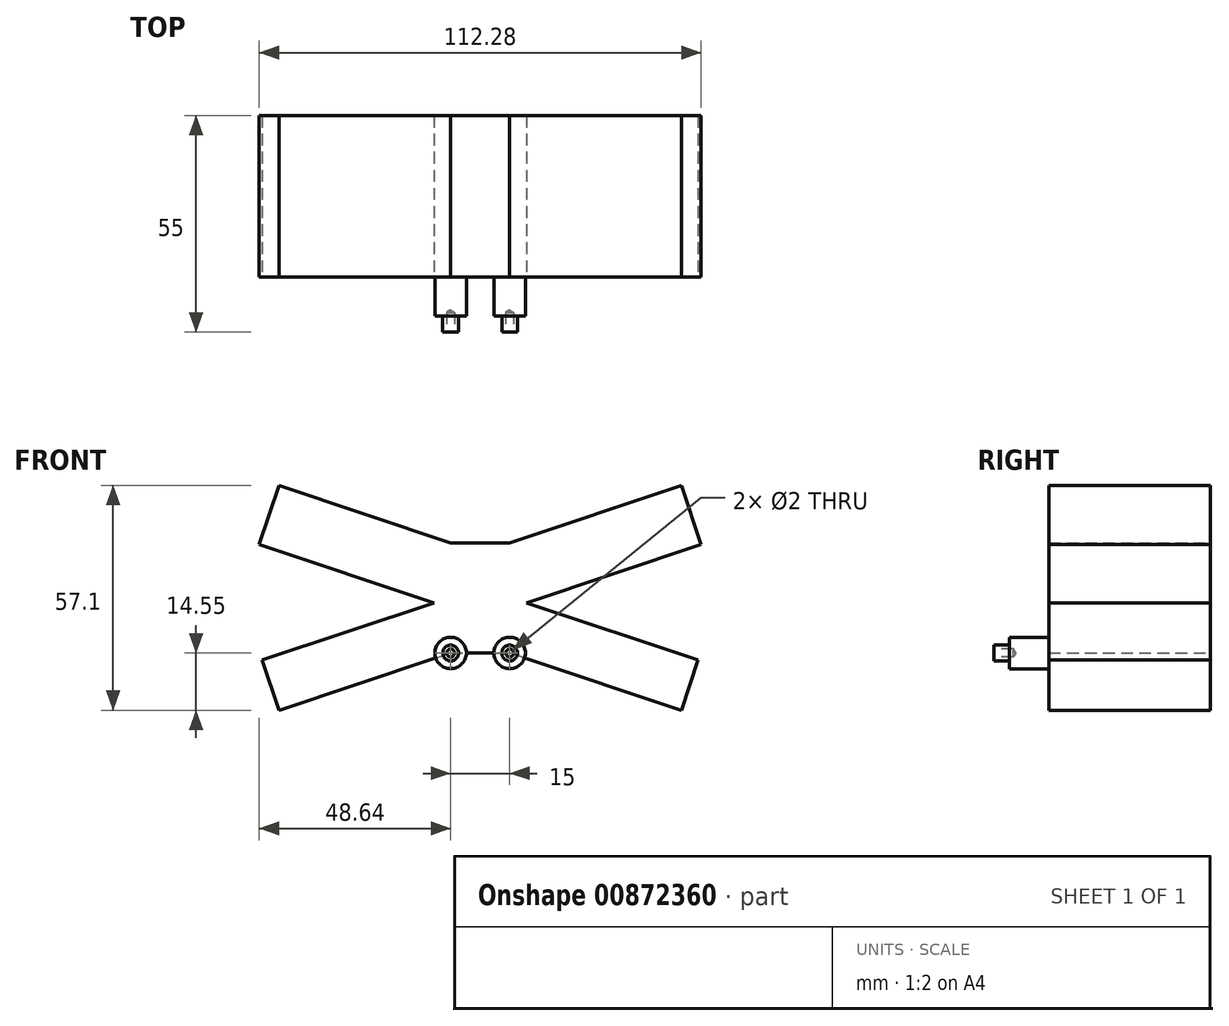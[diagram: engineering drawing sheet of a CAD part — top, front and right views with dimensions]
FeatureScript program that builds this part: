
annotation { "Feature Type Name" : "Feature", "Feature Type Description" : "" }
export const myFeature = defineFeature(function(context is Context, id is Id, definition is map)
    precondition{}
    {
        {
            var Q0;
            Q0=qCreatedBy(makeId("Front.planeOp"),FACE);
            var sketch = newSketch(context, id + "F0", { "sketchPlane" : qUnion([Q0])});
            skLineSegment(sketch, "E0.bottom", {"start": v(0, 0) * mm, "end": v(25, 0) * mm});
            skLineSegment(sketch, "E0.top", {"start": v(0, 28) * mm, "end": v(25, 28) * mm});
            skLineSegment(sketch, "E0.left", {"start": v(0, 0) * mm, "end": v(0, 28) * mm});
            skLineSegment(sketch, "E0.right", {"start": v(25, 0) * mm, "end": v(25, 28) * mm});
            skSolve(sketch);
        }
        {
            var Q0;
            Q0 = qSketchRegion(id + "F0", true);
            var Q1;
            Q1=makeQuery(id+"F0.imprint","IMPRINT",FACE,{"disambiguationData":[TD([[makeQuery(id+"F0.imprint","IMPRINT",EDGE,{"derivedFrom":sQuery(id+"F0.wireOp",EDGE,"E0.bottom")}),1.0]])]});
            extrude(context, id + "F1", {"entities" : qUnion([Q0, Q1]), "depth" : 41 * mm, "offsetDistance" : 25 * mm});
        }
        {
            var Q0;
            Q0=makeQuery(id+"F1.opExtrude","CAP_FACE",FACE,{"disambiguationData":[OSD([sQuery(id+"F0.wireOp",EDGE,"E0.bottom"),sQuery(id+"F0.wireOp",EDGE,"E0.top"),sQuery(id+"F0.wireOp",EDGE,"E0.left"),sQuery(id+"F0.wireOp",EDGE,"E0.right")])],"isStart":false});
            var sketch = newSketch(context, id + "F2", { "sketchPlane" : qUnion([Q0])});
            skCircle(sketch, "E1", {"center": v(25, 0) * mm, "radius": 3.5 * mm});
            skCircle(sketch, "E2", {"center": v(0, 0) * mm, "radius": 3.5 * mm});
            skSolve(sketch);
        }
        {
            var Q0;
            {var subQ0=sQuery(id+"F2.wireOp",EDGE,"E2");var subQ1=makeQuery(id+"F1.opExtrude","CAP_EDGE",EDGE,{"disambiguationData":[OSD([sQuery(id+"F0.wireOp",EDGE,"E0.bottom")])],"isStart":false});var subQ2=makeQuery(id+"F2.imprint","INTERSECT",VERTEX,{"derivedFrom":[subQ1,subQ0]});Q0=makeQuery(id+"F2.imprint","IMPRINT",FACE,{"disambiguationData":[TD([[makeQuery(id+"F2.imprint","IMPRINT",EDGE,{"disambiguationData":[TD([[subQ2,1.0]])],"derivedFrom":subQ0}),1.0]])]});}
            var Q1;
            {var subQ0=sQuery(id+"F2.wireOp",EDGE,"E2");var subQ1=makeQuery(id+"F1.opExtrude","CAP_EDGE",EDGE,{"disambiguationData":[OSD([sQuery(id+"F0.wireOp",EDGE,"E0.bottom")])],"isStart":false});var subQ2=makeQuery(id+"F2.imprint","INTERSECT",VERTEX,{"derivedFrom":[subQ1,subQ0]});Q1=makeQuery(id+"F2.imprint","IMPRINT",FACE,{"disambiguationData":[TD([[makeQuery(id+"F2.imprint","IMPRINT",EDGE,{"disambiguationData":[TD([[subQ2,-1.0]])],"derivedFrom":subQ0}),1.0]])]});}
            var Q2;
            {var subQ0=sQuery(id+"F2.wireOp",EDGE,"E1");var subQ1=makeQuery(id+"F1.opExtrude","CAP_EDGE",EDGE,{"disambiguationData":[OSD([sQuery(id+"F0.wireOp",EDGE,"E0.bottom")])],"isStart":false});var subQ2=makeQuery(id+"F2.imprint","INTERSECT",VERTEX,{"derivedFrom":[subQ1,subQ0]});Q2=makeQuery(id+"F2.imprint","IMPRINT",FACE,{"disambiguationData":[TD([[makeQuery(id+"F2.imprint","IMPRINT",EDGE,{"disambiguationData":[TD([[subQ2,-1.0]])],"derivedFrom":subQ0}),1.0]])]});}
            var Q3;
            {var subQ0=sQuery(id+"F2.wireOp",EDGE,"E1");var subQ1=makeQuery(id+"F1.opExtrude","CAP_EDGE",EDGE,{"disambiguationData":[OSD([sQuery(id+"F0.wireOp",EDGE,"E0.bottom")])],"isStart":false});var subQ2=makeQuery(id+"F2.imprint","INTERSECT",VERTEX,{"derivedFrom":[subQ1,subQ0]});Q3=makeQuery(id+"F2.imprint","IMPRINT",FACE,{"disambiguationData":[TD([[makeQuery(id+"F2.imprint","IMPRINT",EDGE,{"disambiguationData":[TD([[subQ2,1.0]])],"derivedFrom":subQ0}),1.0]])]});}
            extrude(context, id + "F3", {"entities" : qUnion([Q0, Q1, Q2, Q3]), "operationType" : NewBodyOperationType.ADD, "depth" : 8 * mm, "offsetDistance" : 25 * mm});
        }
        {
            var Q0;
            Q0=makeQuery(id+"F3.opExtrude","CAP_FACE",FACE,{"disambiguationData":[OSD([sQuery(id+"F2.wireOp",EDGE,"E2")])],"isStart":false});
            var sketch = newSketch(context, id + "F4", { "sketchPlane" : qUnion([Q0])});
            skCircle(sketch, "E3", {"center": v(0, 0) * mm, "radius": 2 * mm});
            skSolve(sketch);
        }
        {
            var Q0;
            Q0=makeQuery(id+"F4.imprint","IMPRINT",FACE,{"disambiguationData":[TD([[makeQuery(id+"F4.imprint","IMPRINT",EDGE,{"derivedFrom":sQuery(id+"F4.wireOp",EDGE,"E3")}),1.0]])]});
            extrude(context, id + "F5", {"entities" : qUnion([Q0]), "operationType" : NewBodyOperationType.ADD, "depth" : 5 * mm, "offsetDistance" : 25 * mm});
        }
        {
            var Q0;
            Q0=makeQuery(id+"F3.opExtrude","CAP_FACE",FACE,{"disambiguationData":[OSD([sQuery(id+"F2.wireOp",EDGE,"E1")])],"isStart":false});
            var sketch = newSketch(context, id + "F6", { "sketchPlane" : qUnion([Q0])});
            skCircle(sketch, "E4", {"center": v(25, 0) * mm, "radius": 2 * mm});
            skSolve(sketch);
        }
        {
            var Q0;
            Q0=makeQuery(id+"F6.imprint","IMPRINT",FACE,{"disambiguationData":[TD([[makeQuery(id+"F6.imprint","IMPRINT",EDGE,{"derivedFrom":sQuery(id+"F6.wireOp",EDGE,"E4")}),1.0]])]});
            extrude(context, id + "F7", {"entities" : qUnion([Q0]), "operationType" : NewBodyOperationType.ADD, "depth" : 5 * mm, "offsetDistance" : 25 * mm});
        }
        {
            var Q0;
            Q0=makeQuery(id+"F5.opExtrude","CAP_FACE",FACE,{"disambiguationData":[OSD([sQuery(id+"F4.wireOp",EDGE,"E3")])],"isStart":false});
            var sketch = newSketch(context, id + "F8", { "sketchPlane" : qUnion([Q0])});
            skCircle(sketch, "E5", {"center": v(0, 0) * mm, "radius": 1 * mm});
            skSolve(sketch);
        }
        {
            var Q0;
            Q0=sQuery(id+"F8.wireOp",VERTEX,"E5.center");
            var Q1;
            Q1=makeQuery(id+"F1.opExtrude","SWEPT_BODY",BODY,{"disambiguationData":[OSD([sQuery(id+"F0.wireOp",EDGE,"E0.bottom"),sQuery(id+"F0.wireOp",EDGE,"E0.top"),sQuery(id+"F0.wireOp",EDGE,"E0.left"),sQuery(id+"F0.wireOp",EDGE,"E0.right")])]});
            hole(context, id + "F9", {"style" : HoleStyle.SIMPLE, "endStyle" : HoleEndStyle.BLIND, "holeDiameter" : 2 * mm, "majorDiameter" : 5 * mm, "holeDepth" : 5 * mm, "isTappedThrough" : true, "tappedDepth" : 12 * mm, "tapClearance" : 3, "locations" : qUnion([Q0]), "scope" : qUnion([Q1])});
        }
        {
            var Q0;
            Q0=makeQuery(id+"F7.opExtrude","CAP_FACE",FACE,{"disambiguationData":[OSD([sQuery(id+"F6.wireOp",EDGE,"E4")])],"isStart":false});
            var sketch = newSketch(context, id + "F10", { "sketchPlane" : qUnion([Q0])});
            skCircle(sketch, "E6", {"center": v(25, 0) * mm, "radius": 1 * mm});
            skSolve(sketch);
        }
        {
            var Q0;
            Q0=sQuery(id+"F10.wireOp",VERTEX,"E6.center");
            var Q1;
            Q1=makeQuery(id+"F1.opExtrude","SWEPT_BODY",BODY,{"disambiguationData":[OSD([sQuery(id+"F0.wireOp",EDGE,"E0.bottom"),sQuery(id+"F0.wireOp",EDGE,"E0.top"),sQuery(id+"F0.wireOp",EDGE,"E0.left"),sQuery(id+"F0.wireOp",EDGE,"E0.right")])]});
            hole(context, id + "F11", {"style" : HoleStyle.SIMPLE, "endStyle" : HoleEndStyle.BLIND, "holeDiameter" : 2 * mm, "majorDiameter" : 5 * mm, "holeDepth" : 5 * mm, "isTappedThrough" : true, "tappedDepth" : 12 * mm, "tapClearance" : 3, "locations" : qUnion([Q0]), "scope" : qUnion([Q1])});
        }
        {
            var Q0;
            Q0=makeQuery(id+"F1.opExtrude","SWEPT_EDGE",EDGE,{"disambiguationData":[OSD([sQuery(id+"F0.wireOp",EDGE,"E0.top"),sQuery(id+"F0.wireOp",EDGE,"E0.left")])]});
            chamfer(context, id + "F12", {"entities" : qUnion([Q0]), "chamferType" : ChamferType.TWO_OFFSETS, "width1" : 15 * mm, "oppositeDirection" : false, "width2" : 5 * mm, "tangentPropagation" : true});
        }
        {
            var Q0;
            Q0=makeQuery(id+"F1.opExtrude","SWEPT_EDGE",EDGE,{"disambiguationData":[OSD([sQuery(id+"F0.wireOp",EDGE,"E0.top"),sQuery(id+"F0.wireOp",EDGE,"E0.right")])]});
            chamfer(context, id + "F13", {"entities" : qUnion([Q0]), "chamferType" : ChamferType.TWO_OFFSETS, "width1" : 5 * mm, "oppositeDirection" : false, "width2" : 15 * mm, "tangentPropagation" : true});
        }
        {
            var Q0;
            Q0=makeQuery(id+"F13.opChamfer","BLEND_FACE",FACE,{"disambiguationData":[OSD([sQuery(id+"F0.wireOp",EDGE,"E0.top"),sQuery(id+"F0.wireOp",EDGE,"E0.right")])]});
            var sketch = newSketch(context, id + "F14", { "sketchPlane" : qUnion([Q0])});
            skLineSegment(sketch, "E7.bottom", {"start": v(-41, 4.43) * mm, "end": v(0, 4.43) * mm});
            skLineSegment(sketch, "E7.top", {"start": v(-41, 20.24) * mm, "end": v(0, 20.24) * mm});
            skLineSegment(sketch, "E7.left", {"start": v(-41, 4.43) * mm, "end": v(-41, 20.24) * mm});
            skLineSegment(sketch, "E7.right", {"start": v(0, 4.43) * mm, "end": v(0, 20.24) * mm});
            skSolve(sketch);
        }
        {
            var Q0;
            Q0 = qSketchRegion(id + "F14", true);
            extrude(context, id + "F15", {"entities" : qUnion([Q0]), "operationType" : NewBodyOperationType.ADD, "depth" : 46 * mm, "offsetDistance" : 25 * mm});
        }
        {
            var Q0;
            Q0=makeQuery(id+"F12.opChamfer","BLEND_FACE",FACE,{"disambiguationData":[OSD([sQuery(id+"F0.wireOp",EDGE,"E0.top"),sQuery(id+"F0.wireOp",EDGE,"E0.left")])]});
            var sketch = newSketch(context, id + "F16", { "sketchPlane" : qUnion([Q0])});
            skLineSegment(sketch, "E8.bottom", {"start": v(0, 12.33) * mm, "end": v(41, 12.33) * mm});
            skLineSegment(sketch, "E8.top", {"start": v(0, 28.14) * mm, "end": v(41, 28.14) * mm});
            skLineSegment(sketch, "E8.left", {"start": v(0, 12.33) * mm, "end": v(0, 28.14) * mm});
            skLineSegment(sketch, "E8.right", {"start": v(41, 12.33) * mm, "end": v(41, 28.14) * mm});
            skSolve(sketch);
        }
        {
            var Q0;
            Q0 = qSketchRegion(id + "F16", true);
            extrude(context, id + "F17", {"entities" : qUnion([Q0]), "operationType" : NewBodyOperationType.ADD, "depth" : 46 * mm, "offsetDistance" : 25 * mm});
        }
        {
            var Q0;
            Q0=makeQuery(id+"F1.opExtrude","SWEPT_EDGE",EDGE,{"disambiguationData":[OSD([sQuery(id+"F0.wireOp",EDGE,"E0.bottom"),sQuery(id+"F0.wireOp",EDGE,"E0.right")])]});
            chamfer(context, id + "F18", {"entities" : qUnion([Q0]), "chamferType" : ChamferType.TWO_OFFSETS, "width1" : 15 * mm, "oppositeDirection" : false, "width2" : 5 * mm, "tangentPropagation" : true});
        }
        {
            var Q0;
            Q0=makeQuery(id+"F18.opChamfer","BLEND_FACE",FACE,{"disambiguationData":[OSD([sQuery(id+"F0.wireOp",EDGE,"E0.bottom"),sQuery(id+"F0.wireOp",EDGE,"E0.right")])]});
            var sketch = newSketch(context, id + "F19", { "sketchPlane" : qUnion([Q0])});
            skLineSegment(sketch, "E9.bottom", {"start": v(-41, 6.32) * mm, "end": v(0, 6.32) * mm});
            skLineSegment(sketch, "E9.top", {"start": v(-41, 19.76) * mm, "end": v(0, 19.76) * mm});
            skLineSegment(sketch, "E9.left", {"start": v(-41, 6.32) * mm, "end": v(-41, 19.76) * mm});
            skLineSegment(sketch, "E9.right", {"start": v(0, 6.32) * mm, "end": v(0, 19.76) * mm});
            skSolve(sketch);
        }
        {
            var Q0;
            Q0 = qSketchRegion(id + "F19", true);
            extrude(context, id + "F20", {"entities" : qUnion([Q0]), "operationType" : NewBodyOperationType.ADD, "depth" : 46 * mm, "offsetDistance" : 25 * mm});
        }
        {
            var Q0;
            Q0=makeQuery(id+"F1.opExtrude","SWEPT_EDGE",EDGE,{"disambiguationData":[OSD([sQuery(id+"F0.wireOp",EDGE,"E0.bottom"),sQuery(id+"F0.wireOp",EDGE,"E0.left")])]});
            chamfer(context, id + "F21", {"entities" : qUnion([Q0]), "chamferType" : ChamferType.TWO_OFFSETS, "width1" : 5 * mm, "oppositeDirection" : false, "width2" : 15 * mm, "tangentPropagation" : true});
        }
        {
            var Q0;
            Q0=makeQuery(id+"F21.opChamfer","BLEND_FACE",FACE,{"disambiguationData":[OSD([sQuery(id+"F0.wireOp",EDGE,"E0.bottom"),sQuery(id+"F0.wireOp",EDGE,"E0.left")])]});
            var sketch = newSketch(context, id + "F22", { "sketchPlane" : qUnion([Q0])});
            skLineSegment(sketch, "E10.bottom", {"start": v(0, -1.58) * mm, "end": v(41, -1.58) * mm});
            skLineSegment(sketch, "E10.top", {"start": v(0, 11.86) * mm, "end": v(41, 11.86) * mm});
            skLineSegment(sketch, "E10.left", {"start": v(0, -1.58) * mm, "end": v(0, 11.86) * mm});
            skLineSegment(sketch, "E10.right", {"start": v(41, -1.58) * mm, "end": v(41, 11.86) * mm});
            skSolve(sketch);
        }
        {
            var Q0;
            Q0 = qSketchRegion(id + "F22", true);
            extrude(context, id + "F23", {"entities" : qUnion([Q0]), "operationType" : NewBodyOperationType.ADD, "depth" : 46 * mm, "offsetDistance" : 25 * mm});
        }
        {
            var Q0;
            Q0=makeQuery(id+"F23.boolean.opBoolean","MERGE",FACE,{"derivedFrom":[makeQuery(id+"F20.boolean.opBoolean","MERGE",FACE,{"derivedFrom":[makeQuery(id+"F17.boolean.opBoolean","MERGE",FACE,{"derivedFrom":[makeQuery(id+"F15.boolean.opBoolean","MERGE",FACE,{"derivedFrom":[makeQuery(id+"F1.opExtrude","CAP_FACE",FACE,{"disambiguationData":[OSD([sQuery(id+"F0.wireOp",EDGE,"E0.bottom"),sQuery(id+"F0.wireOp",EDGE,"E0.top"),sQuery(id+"F0.wireOp",EDGE,"E0.left"),sQuery(id+"F0.wireOp",EDGE,"E0.right")])],"isStart":false}),makeQuery(id+"F15.opExtrude","SWEPT_FACE",FACE,{"disambiguationData":[OSD([sQuery(id+"F14.wireOp",EDGE,"E7.left")])]})]}),makeQuery(id+"F17.opExtrude","SWEPT_FACE",FACE,{"disambiguationData":[OSD([sQuery(id+"F16.wireOp",EDGE,"E8.right")])]})]}),makeQuery(id+"F20.opExtrude","SWEPT_FACE",FACE,{"disambiguationData":[OSD([sQuery(id+"F19.wireOp",EDGE,"E9.left")])]})]}),makeQuery(id+"F23.opExtrude","SWEPT_FACE",FACE,{"disambiguationData":[OSD([sQuery(id+"F22.wireOp",EDGE,"E10.right")])]})]});
            var sketch = newSketch(context, id + "F24", { "sketchPlane" : qUnion([Q0])});
            skCircle(sketch, "E11", {"center": v(20, 0) * mm, "radius": 4 * mm});
            skCircle(sketch, "E12", {"center": v(5, 0) * mm, "radius": 4 * mm});
            skSolve(sketch);
        }
        {
            var Q0;
            {var subQ0=sQuery(id+"F24.wireOp",EDGE,"E11");var subQ1=makeQuery(id+"F20.opExtrude","SWEPT_EDGE",EDGE,{"disambiguationData":[OSD([sQuery(id+"F19.wireOp",EDGE,"E9.bottom"),sQuery(id+"F19.wireOp",EDGE,"E9.left")])]});var subQ2=makeQuery(id+"F24.imprint","INTERSECT",VERTEX,{"derivedFrom":[subQ1,subQ0]});Q0=makeQuery(id+"F24.imprint","IMPRINT",FACE,{"disambiguationData":[TD([[makeQuery(id+"F24.imprint","IMPRINT",EDGE,{"disambiguationData":[TD([[subQ2,-1.0]])],"derivedFrom":subQ0}),1.0]])]});}
            var Q1;
            {var subQ0=sQuery(id+"F24.wireOp",EDGE,"E12");var subQ4=makeQuery(id+"F23.opExtrude","SWEPT_EDGE",EDGE,{"disambiguationData":[OSD([sQuery(id+"F22.wireOp",EDGE,"E10.bottom"),sQuery(id+"F22.wireOp",EDGE,"E10.right")])]});var subQ5=makeQuery(id+"F24.imprint","INTERSECT",VERTEX,{"derivedFrom":[subQ4,subQ0]});Q1=makeQuery(id+"F24.imprint","IMPRINT",FACE,{"disambiguationData":[TD([[makeQuery(id+"F24.imprint","IMPRINT",EDGE,{"disambiguationData":[TD([[subQ5,1.0]])],"derivedFrom":subQ0}),1.0]])]});}
            var Q2;
            {var subQ0=sQuery(id+"F24.wireOp",EDGE,"E11");var subQ1=makeQuery(id+"F20.opExtrude","SWEPT_EDGE",EDGE,{"disambiguationData":[OSD([sQuery(id+"F19.wireOp",EDGE,"E9.bottom"),sQuery(id+"F19.wireOp",EDGE,"E9.left")])]});var subQ2=makeQuery(id+"F24.imprint","INTERSECT",VERTEX,{"derivedFrom":[subQ1,subQ0]});Q2=makeQuery(id+"F24.imprint","IMPRINT",FACE,{"disambiguationData":[TD([[makeQuery(id+"F24.imprint","IMPRINT",EDGE,{"disambiguationData":[TD([[subQ2,1.0]])],"derivedFrom":subQ0}),1.0]])]});}
            var Q3;
            {var subQ0=sQuery(id+"F24.wireOp",EDGE,"E12");var subQ4=makeQuery(id+"F23.opExtrude","SWEPT_EDGE",EDGE,{"disambiguationData":[OSD([sQuery(id+"F22.wireOp",EDGE,"E10.bottom"),sQuery(id+"F22.wireOp",EDGE,"E10.right")])]});var subQ5=makeQuery(id+"F24.imprint","INTERSECT",VERTEX,{"derivedFrom":[subQ4,subQ0]});Q3=makeQuery(id+"F24.imprint","IMPRINT",FACE,{"disambiguationData":[TD([[makeQuery(id+"F24.imprint","IMPRINT",EDGE,{"disambiguationData":[TD([[subQ5,-1.0]])],"derivedFrom":subQ0}),1.0]])]});}
            extrude(context, id + "F25", {"entities" : qUnion([Q0, Q1, Q2, Q3]), "operationType" : NewBodyOperationType.ADD, "depth" : 10 * mm, "offsetDistance" : 25 * mm});
        }
        {
            var Q0;
            Q0=makeQuery(id+"F25.opExtrude","CAP_FACE",FACE,{"disambiguationData":[OSD([sQuery(id+"F24.wireOp",EDGE,"E12")])],"isStart":false});
            var sketch = newSketch(context, id + "F26", { "sketchPlane" : qUnion([Q0])});
            skCircle(sketch, "E13", {"center": v(5, 0) * mm, "radius": 2 * mm});
            skSolve(sketch);
        }
        {
            var Q0;
            Q0 = qSketchRegion(id + "F26", true);
            extrude(context, id + "F27", {"entities" : qUnion([Q0]), "operationType" : NewBodyOperationType.ADD, "depth" : 4 * mm, "offsetDistance" : 25 * mm});
        }
        {
            var Q0;
            Q0=makeQuery(id+"F25.opExtrude","CAP_FACE",FACE,{"disambiguationData":[OSD([sQuery(id+"F24.wireOp",EDGE,"E11")])],"isStart":false});
            var sketch = newSketch(context, id + "F28", { "sketchPlane" : qUnion([Q0])});
            skCircle(sketch, "E14", {"center": v(20, 0) * mm, "radius": 2 * mm});
            skSolve(sketch);
        }
        {
            var Q0;
            Q0=makeQuery(id+"F28.imprint","IMPRINT",FACE,{"disambiguationData":[TD([[makeQuery(id+"F28.imprint","IMPRINT",EDGE,{"derivedFrom":sQuery(id+"F28.wireOp",EDGE,"E14")}),1.0]])]});
            extrude(context, id + "F29", {"entities" : qUnion([Q0]), "operationType" : NewBodyOperationType.ADD, "depth" : 4 * mm, "offsetDistance" : 25 * mm});
        }
        {
            var Q0;
            Q0=makeQuery(id+"F27.opExtrude","CAP_FACE",FACE,{"disambiguationData":[OSD([sQuery(id+"F26.wireOp",EDGE,"E13")])],"isStart":false});
            var sketch = newSketch(context, id + "F30", { "sketchPlane" : qUnion([Q0])});
            skCircle(sketch, "E15", {"center": v(5, 0) * mm, "radius": 1 * mm});
            skSolve(sketch);
        }
        {
            var Q0;
            Q0=sQuery(id+"F30.wireOp",VERTEX,"E15.center");
            var Q1;
            Q1=makeQuery(id+"F1.opExtrude","SWEPT_BODY",BODY,{"disambiguationData":[OSD([sQuery(id+"F0.wireOp",EDGE,"E0.bottom"),sQuery(id+"F0.wireOp",EDGE,"E0.top"),sQuery(id+"F0.wireOp",EDGE,"E0.left"),sQuery(id+"F0.wireOp",EDGE,"E0.right")])]});
            hole(context, id + "F31", {"style" : HoleStyle.SIMPLE, "endStyle" : HoleEndStyle.BLIND, "holeDiameter" : 2 * mm, "majorDiameter" : 5 * mm, "holeDepth" : 5 * mm, "isTappedThrough" : true, "tappedDepth" : 12 * mm, "tapClearance" : 3, "locations" : qUnion([Q0]), "scope" : qUnion([Q1])});
        }
        {
            var Q0;
            Q0=makeQuery(id+"F29.opExtrude","CAP_FACE",FACE,{"disambiguationData":[OSD([sQuery(id+"F28.wireOp",EDGE,"E14")])],"isStart":false});
            var sketch = newSketch(context, id + "F32", { "sketchPlane" : qUnion([Q0])});
            skCircle(sketch, "E16", {"center": v(20, 0) * mm, "radius": 1 * mm});
            skSolve(sketch);
        }
        {
            var Q0;
            Q0=sQuery(id+"F32.wireOp",VERTEX,"E16.center");
            var Q1;
            Q1=makeQuery(id+"F1.opExtrude","SWEPT_BODY",BODY,{"disambiguationData":[OSD([sQuery(id+"F0.wireOp",EDGE,"E0.bottom"),sQuery(id+"F0.wireOp",EDGE,"E0.top"),sQuery(id+"F0.wireOp",EDGE,"E0.left"),sQuery(id+"F0.wireOp",EDGE,"E0.right")])]});
            hole(context, id + "F33", {"style" : HoleStyle.SIMPLE, "endStyle" : HoleEndStyle.BLIND, "holeDiameter" : 2 * mm, "majorDiameter" : 5 * mm, "holeDepth" : 5 * mm, "isTappedThrough" : true, "tappedDepth" : 12 * mm, "tapClearance" : 3, "locations" : qUnion([Q0]), "scope" : qUnion([Q1])});
        }
    });
